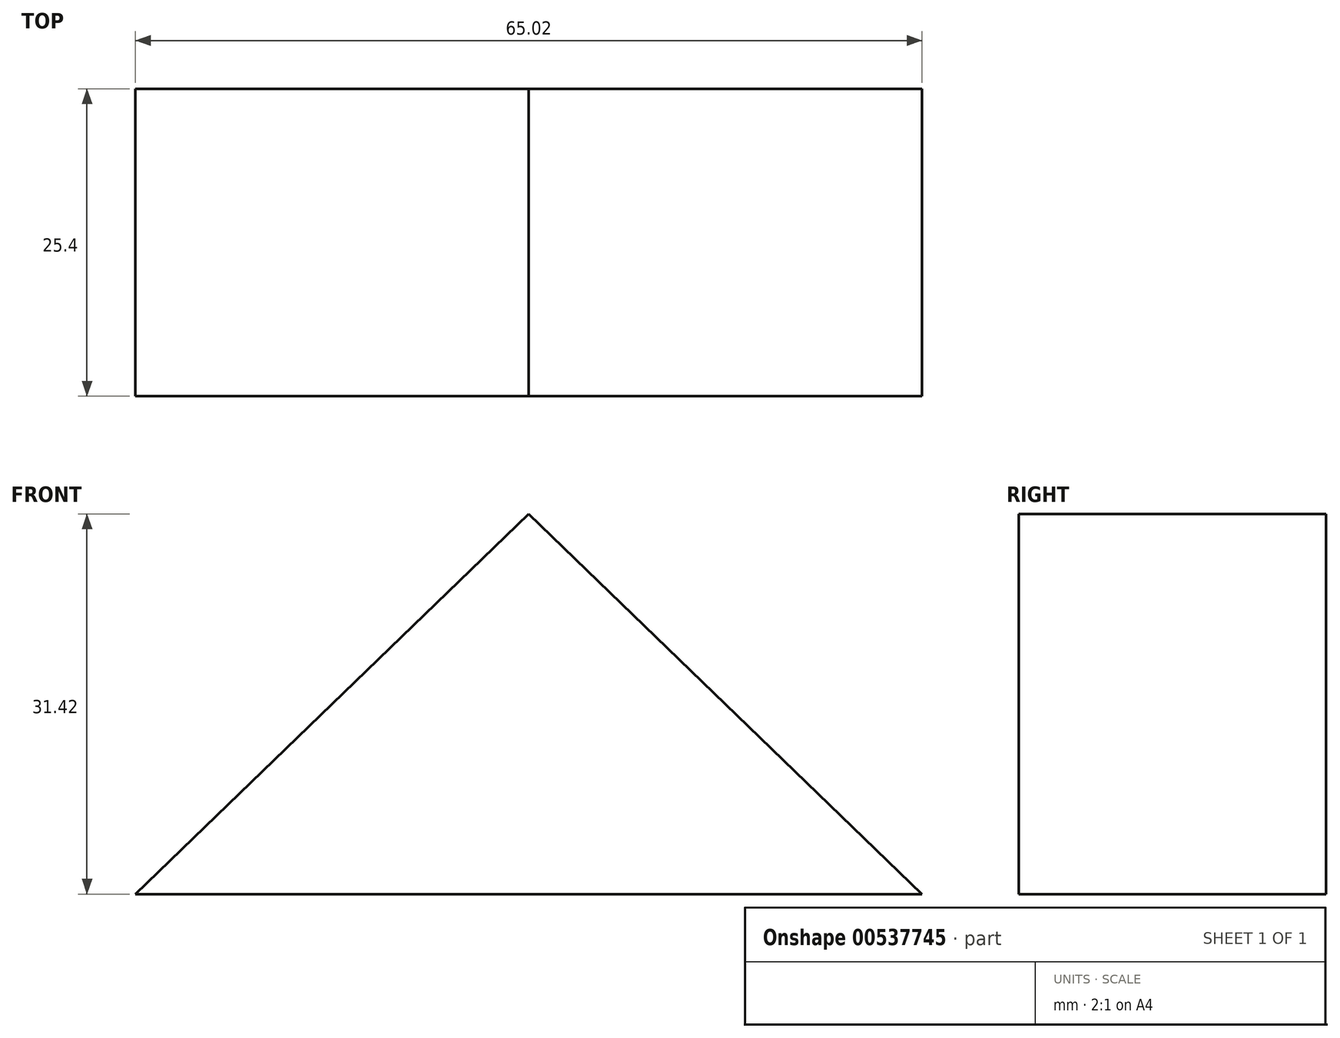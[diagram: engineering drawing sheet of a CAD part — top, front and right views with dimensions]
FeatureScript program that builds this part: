
annotation { "Feature Type Name" : "Feature", "Feature Type Description" : "" }
export const myFeature = defineFeature(function(context is Context, id is Id, definition is map)
    precondition{}
    {
        {
            var Q0;
            Q0=qCreatedBy(makeId("Front.planeOp"),FACE);
            var sketch = newSketch(context, id + "F0", { "sketchPlane" : qUnion([Q0])});
            skLineSegment(sketch, "E0", {"start": v(-32.51, 0) * mm, "end": v(0, 31.42) * mm});
            skLineSegment(sketch, "E1", {"start": v(0, 31.42) * mm, "end": v(32.51, 0) * mm});
            skLineSegment(sketch, "E2", {"start": v(-32.51, 0) * mm, "end": v(32.51, 0) * mm});
            skLineSegment(sketch, "E3", {"start": v(0, 0) * mm, "end": v(0, 31.42) * mm});
            skSolve(sketch);
        }
        {
            var Q0;
            Q0 = qSketchRegion(id + "F0", true);
            extrude(context, id + "F1", {"entities" : qUnion([Q0]), "depth" : 25.4 * mm, "offsetDistance" : 25.4 * mm});
        }
    });
